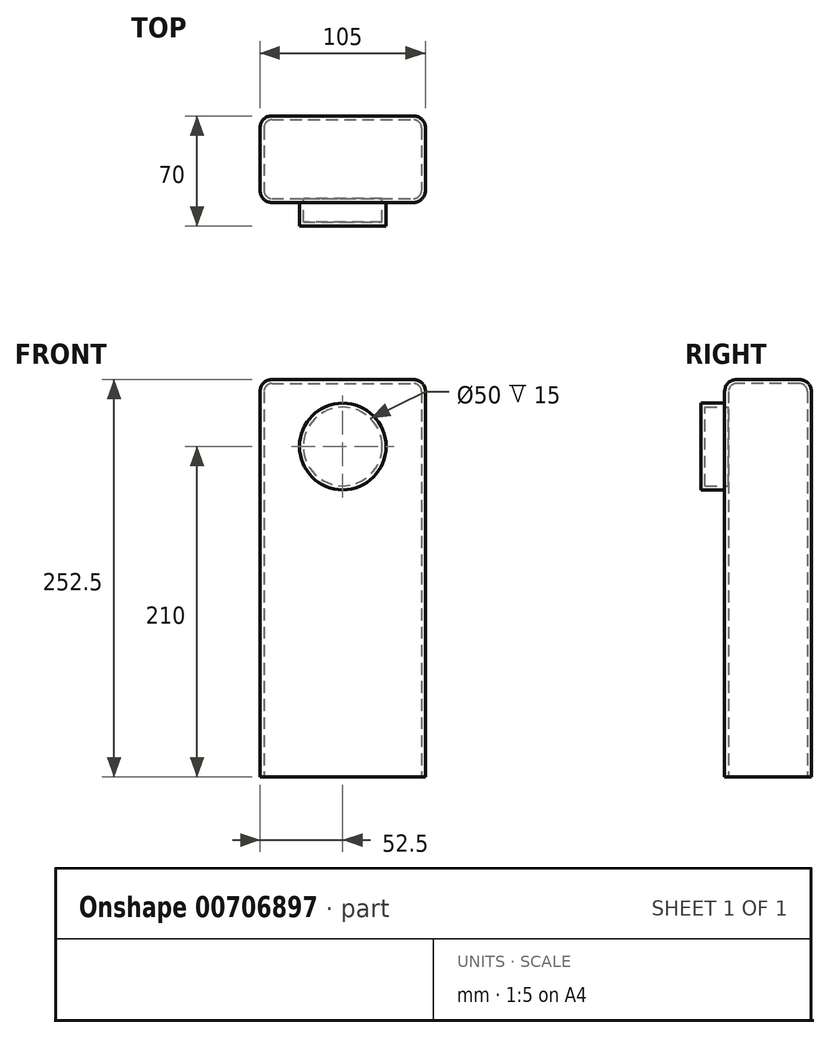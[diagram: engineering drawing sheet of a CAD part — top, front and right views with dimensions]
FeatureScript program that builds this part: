
annotation { "Feature Type Name" : "Feature", "Feature Type Description" : "" }
export const myFeature = defineFeature(function(context is Context, id is Id, definition is map)
    precondition{}
    {
        {
            var Q0;
            Q0=qCreatedBy(makeId("Top.planeOp"),FACE);
            var sketch = newSketch(context, id + "F0", { "sketchPlane" : qUnion([Q0])});
            skLineSegment(sketch, "E0.bottom", {"start": v(-50, 25) * mm, "end": v(50, 25) * mm});
            skLineSegment(sketch, "E0.top", {"start": v(-50, -25) * mm, "end": v(50, -25) * mm});
            skLineSegment(sketch, "E0.left", {"start": v(-50, 25) * mm, "end": v(-50, -25) * mm});
            skLineSegment(sketch, "E0.right", {"start": v(50, 25) * mm, "end": v(50, -25) * mm});
            skSolve(sketch);
        }
        {
            var Q0;
            Q0=makeQuery(id+"F0.imprint","IMPRINT",FACE,{"disambiguationData":[TD([[makeQuery(id+"F0.imprint","IMPRINT",EDGE,{"derivedFrom":sQuery(id+"F0.wireOp",EDGE,"E0.bottom")}),-1.0]])]});
            extrude(context, id + "F1", {"entities" : qUnion([Q0]), "depth" : 250 * mm, "offsetDistance" : 25 * mm});
        }
        {
            var Q0;
            Q0=makeQuery(id+"F1.opExtrude","SWEPT_FACE",FACE,{"disambiguationData":[OSD([sQuery(id+"F0.wireOp",EDGE,"E0.top")])]});
            var sketch = newSketch(context, id + "F2", { "sketchPlane" : qUnion([Q0])});
            skCircle(sketch, "E1", {"center": v(0, 210) * mm, "radius": 25 * mm});
            skSolve(sketch);
        }
        {
            var Q0;
            Q0 = qSketchRegion(id + "F2", true);
            extrude(context, id + "F3", {"entities" : qUnion([Q0]), "operationType" : NewBodyOperationType.ADD, "depth" : 15 * mm, "offsetDistance" : 25 * mm});
        }
        {
            var Q0;
            Q0=makeQuery(id+"F1.opExtrude","CAP_EDGE",EDGE,{"disambiguationData":[OSD([sQuery(id+"F0.wireOp",EDGE,"E0.left")])],"isStart":false});
            var Q1;
            Q1=makeQuery(id+"F1.opExtrude","CAP_EDGE",EDGE,{"disambiguationData":[OSD([sQuery(id+"F0.wireOp",EDGE,"E0.bottom")])],"isStart":false});
            var Q2;
            Q2=makeQuery(id+"F1.opExtrude","CAP_EDGE",EDGE,{"disambiguationData":[OSD([sQuery(id+"F0.wireOp",EDGE,"E0.right")])],"isStart":false});
            var Q3;
            Q3=makeQuery(id+"F1.opExtrude","CAP_EDGE",EDGE,{"disambiguationData":[OSD([sQuery(id+"F0.wireOp",EDGE,"E0.top")])],"isStart":false});
            var Q4;
            Q4=makeQuery(id+"F1.opExtrude","SWEPT_EDGE",EDGE,{"disambiguationData":[OSD([sQuery(id+"F0.wireOp",EDGE,"E0.top"),sQuery(id+"F0.wireOp",EDGE,"E0.right")])]});
            var Q5;
            Q5=makeQuery(id+"F1.opExtrude","SWEPT_EDGE",EDGE,{"disambiguationData":[OSD([sQuery(id+"F0.wireOp",EDGE,"E0.bottom"),sQuery(id+"F0.wireOp",EDGE,"E0.right")])]});
            var Q6;
            Q6=makeQuery(id+"F1.opExtrude","SWEPT_EDGE",EDGE,{"disambiguationData":[OSD([sQuery(id+"F0.wireOp",EDGE,"E0.top"),sQuery(id+"F0.wireOp",EDGE,"E0.left")])]});
            var Q7;
            Q7=makeQuery(id+"F1.opExtrude","SWEPT_EDGE",EDGE,{"disambiguationData":[OSD([sQuery(id+"F0.wireOp",EDGE,"E0.bottom"),sQuery(id+"F0.wireOp",EDGE,"E0.left")])]});
            fillet(context, id + "F4", {"entities" : qUnion([Q0, Q1, Q2, Q3, Q4, Q5, Q6, Q7]), "radius" : 5 * mm, "tangentPropagation" : true, "allowEdgeOverflow" : false});
        }
        {
            var Q0;
            Q0=makeQuery(id+"F1.opExtrude","CAP_FACE",FACE,{"disambiguationData":[OSD([sQuery(id+"F0.wireOp",EDGE,"E0.bottom"),sQuery(id+"F0.wireOp",EDGE,"E0.top"),sQuery(id+"F0.wireOp",EDGE,"E0.left"),sQuery(id+"F0.wireOp",EDGE,"E0.right")])],"isStart":true});
            shell(context, id + "F5", {"entities" : qUnion([Q0]), "thickness" : 2.5 * mm, "oppositeDirection" : true});
        }
    });
